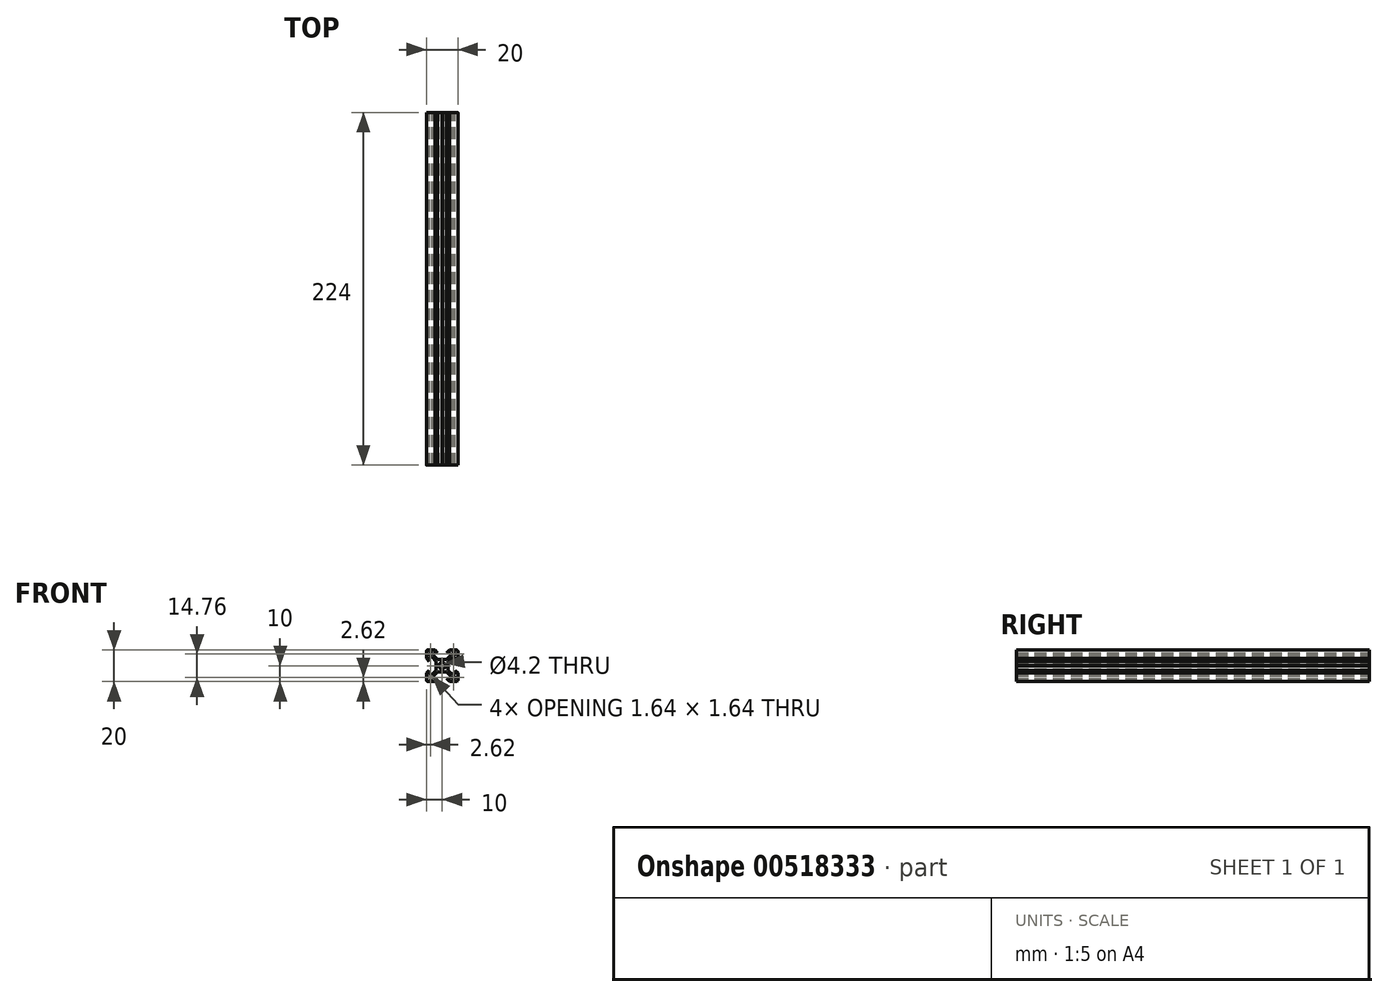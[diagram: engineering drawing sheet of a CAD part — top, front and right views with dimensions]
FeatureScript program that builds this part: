
annotation { "Feature Type Name" : "Feature", "Feature Type Description" : "" }
export const myFeature = defineFeature(function(context is Context, id is Id, definition is map)
    precondition{}
    {
        {
            var Q0;
            Q0=qCreatedBy(makeId("Front.planeOp"),FACE);
            var sketch = newSketch(context, id + "F0", { "sketchPlane" : qUnion([Q0])});
            skLineSegment(sketch, "E0.rect.bottom", {"start": v(-9, 10) * mm, "end": v(9, 10) * mm});
            skLineSegment(sketch, "E0.rect.top", {"start": v(-9, -10) * mm, "end": v(9, -10) * mm});
            skLineSegment(sketch, "E0.rect.left", {"start": v(-10, 9) * mm, "end": v(-10, -9) * mm});
            skLineSegment(sketch, "E0.rect.right", {"start": v(10, 9) * mm, "end": v(10, -9) * mm});
            skPoint(sketch, "E0.rect.middle", {"position": v(0, 0) * mm});
            skCircle(sketch, "E1", {"center": v(0, 0) * mm, "radius": 2.1 * mm});
            skPoint(sketch, "E2.visualSharp", {"position": v(-10, 10) * mm});
            skArc(sketch, "E2.filletArc", {"start": v(-9, 10) * mm, "mid": v(-9.7, 9.7) * mm, "end": v(-10, 9) * mm});
            skPoint(sketch, "E3.visualSharp", {"position": v(10, 10) * mm});
            skArc(sketch, "E3.filletArc", {"start": v(10, 9) * mm, "mid": v(9.7, 9.7) * mm, "end": v(9, 10) * mm});
            skPoint(sketch, "E4.visualSharp", {"position": v(10, -10) * mm});
            skArc(sketch, "E4.filletArc", {"start": v(9, -10) * mm, "mid": v(9.7, -9.7) * mm, "end": v(10, -9) * mm});
            skPoint(sketch, "E5.visualSharp", {"position": v(-10, -10) * mm});
            skArc(sketch, "E5.filletArc", {"start": v(-10, -9) * mm, "mid": v(-9.7, -9.7) * mm, "end": v(-9, -10) * mm});
            skLineSegment(sketch, "E6", {"start": v(10, 10) * mm, "end": v(-10, -10) * mm, "construction": true});
            skLineSegment(sketch, "E7", {"start": v(-10, 10) * mm, "end": v(10, -10) * mm, "construction": true});
            skLineSegment(sketch, "E8", {"start": v(-4.64, 10) * mm, "end": v(-2.84, 8.2) * mm});
            skLineSegment(sketch, "E9", {"start": v(-2.84, 8.2) * mm, "end": v(-5.5, 8.2) * mm});
            skLineSegment(sketch, "E10", {"start": v(-5.5, 8.2) * mm, "end": v(-5.5, 6.56) * mm});
            skLineSegment(sketch, "E11", {"start": v(-5.5, 6.56) * mm, "end": v(-2.84, 3.9) * mm});
            skLineSegment(sketch, "E12.MirrorCS", {"start": v(4.64, 10) * mm, "end": v(2.84, 8.2) * mm});
            skLineSegment(sketch, "E13.MirrorCS", {"start": v(2.84, 8.2) * mm, "end": v(5.5, 8.2) * mm});
            skLineSegment(sketch, "E14.MirrorCS", {"start": v(5.5, 8.2) * mm, "end": v(5.5, 6.56) * mm});
            skLineSegment(sketch, "E15.MirrorCS", {"start": v(5.5, 6.56) * mm, "end": v(2.84, 3.9) * mm});
            skLineSegment(sketch, "E16", {"start": v(-2.84, 3.9) * mm, "end": v(2.84, 3.9) * mm});
            skLineSegment(sketch, "E17.MirrorCS", {"start": v(-4.64, -10) * mm, "end": v(-2.84, -8.2) * mm});
            skLineSegment(sketch, "E18.MirrorCS", {"start": v(-2.84, -8.2) * mm, "end": v(-5.5, -8.2) * mm});
            skLineSegment(sketch, "E19.MirrorCS", {"start": v(-5.5, -8.2) * mm, "end": v(-5.5, -6.56) * mm});
            skLineSegment(sketch, "E20.MirrorCS", {"start": v(-5.5, -6.56) * mm, "end": v(-2.84, -3.9) * mm});
            skLineSegment(sketch, "E21.MirrorCS", {"start": v(-2.84, -3.9) * mm, "end": v(2.84, -3.9) * mm});
            skLineSegment(sketch, "E22.MirrorCS", {"start": v(5.5, -6.56) * mm, "end": v(2.84, -3.9) * mm});
            skLineSegment(sketch, "E23.MirrorCS", {"start": v(5.5, -8.2) * mm, "end": v(5.5, -6.56) * mm});
            skLineSegment(sketch, "E24.MirrorCS", {"start": v(2.84, -8.2) * mm, "end": v(5.5, -8.2) * mm});
            skLineSegment(sketch, "E25.MirrorCS", {"start": v(4.64, -10) * mm, "end": v(2.84, -8.2) * mm});
            skLineSegment(sketch, "E26.MirrorCS", {"start": v(10, -4.64) * mm, "end": v(8.2, -2.84) * mm});
            skLineSegment(sketch, "E27.MirrorCS", {"start": v(8.2, -2.84) * mm, "end": v(8.2, -5.5) * mm});
            skLineSegment(sketch, "E28.MirrorCS", {"start": v(8.2, -5.5) * mm, "end": v(6.56, -5.5) * mm});
            skLineSegment(sketch, "E29.MirrorCS", {"start": v(6.56, -5.5) * mm, "end": v(3.9, -2.84) * mm});
            skLineSegment(sketch, "E30.MirrorCS", {"start": v(3.9, -2.84) * mm, "end": v(3.9, 2.84) * mm});
            skLineSegment(sketch, "E31.MirrorCS", {"start": v(6.56, 5.5) * mm, "end": v(3.9, 2.84) * mm});
            skLineSegment(sketch, "E32.MirrorCS", {"start": v(8.2, 5.5) * mm, "end": v(6.56, 5.5) * mm});
            skLineSegment(sketch, "E33.MirrorCS", {"start": v(8.2, 2.84) * mm, "end": v(8.2, 5.5) * mm});
            skLineSegment(sketch, "E34.MirrorCS", {"start": v(10, 4.64) * mm, "end": v(8.2, 2.84) * mm});
            skLineSegment(sketch, "E35.MirrorCS", {"start": v(-8.2, 2.84) * mm, "end": v(-8.2, 5.5) * mm});
            skLineSegment(sketch, "E36.MirrorCS", {"start": v(-10, 4.64) * mm, "end": v(-8.2, 2.84) * mm});
            skLineSegment(sketch, "E37.MirrorCS", {"start": v(-8.2, 5.5) * mm, "end": v(-6.56, 5.5) * mm});
            skLineSegment(sketch, "E38.MirrorCS", {"start": v(-6.56, 5.5) * mm, "end": v(-3.9, 2.84) * mm});
            skLineSegment(sketch, "E39.MirrorCS", {"start": v(-3.9, 2.84) * mm, "end": v(-3.9, -2.84) * mm});
            skLineSegment(sketch, "E40.MirrorCS", {"start": v(-6.56, -5.5) * mm, "end": v(-3.9, -2.84) * mm});
            skLineSegment(sketch, "E41.MirrorCS", {"start": v(-8.2, -5.5) * mm, "end": v(-6.56, -5.5) * mm});
            skLineSegment(sketch, "E42.MirrorCS", {"start": v(-8.2, -2.84) * mm, "end": v(-8.2, -5.5) * mm});
            skLineSegment(sketch, "E43.MirrorCS", {"start": v(-10, -4.64) * mm, "end": v(-8.2, -2.84) * mm});
            skLineSegment(sketch, "E44", {"start": v(-8.05, 8.2) * mm, "end": v(-6.71, 8.2) * mm});
            skLineSegment(sketch, "E45", {"start": v(-6.56, 8.05) * mm, "end": v(-6.56, 8.05) * mm});
            skLineSegment(sketch, "E46", {"start": v(-6.6, 7.94) * mm, "end": v(-7.94, 6.6) * mm});
            skLineSegment(sketch, "E47", {"start": v(-8.05, 6.56) * mm, "end": v(-8.05, 6.56) * mm});
            skLineSegment(sketch, "E48", {"start": v(-8.2, 6.71) * mm, "end": v(-8.2, 8.05) * mm});
            skLineSegment(sketch, "E49.MirrorCS", {"start": v(8.2, 6.71) * mm, "end": v(8.2, 8.05) * mm});
            skLineSegment(sketch, "E50.MirrorCS", {"start": v(7.99, 6.56) * mm, "end": v(8.05, 6.56) * mm});
            skLineSegment(sketch, "E51.MirrorCS", {"start": v(6.56, 7.99) * mm, "end": v(7.99, 6.56) * mm});
            skLineSegment(sketch, "E52.MirrorCS", {"start": v(6.56, 8.05) * mm, "end": v(6.56, 7.99) * mm});
            skLineSegment(sketch, "E53.MirrorCS", {"start": v(8.05, 8.2) * mm, "end": v(6.7, 8.2) * mm});
            skLineSegment(sketch, "E54.MirrorCS", {"start": v(-8.2, -6.71) * mm, "end": v(-8.2, -8.2) * mm});
            skLineSegment(sketch, "E55.MirrorCS", {"start": v(-7.99, -6.56) * mm, "end": v(-8.05, -6.56) * mm});
            skLineSegment(sketch, "E56.MirrorCS", {"start": v(-6.6, -7.94) * mm, "end": v(-7.99, -6.56) * mm});
            skLineSegment(sketch, "E57.MirrorCS", {"start": v(-6.56, -8.05) * mm, "end": v(-6.56, -8.05) * mm});
            skLineSegment(sketch, "E58.MirrorCS", {"start": v(-8.2, -8.2) * mm, "end": v(-6.7, -8.2) * mm});
            skLineSegment(sketch, "E59.MirrorCS", {"start": v(6.56, -8.05) * mm, "end": v(6.56, -7.99) * mm});
            skLineSegment(sketch, "E60.MirrorCS", {"start": v(6.56, -7.99) * mm, "end": v(7.94, -6.6) * mm});
            skLineSegment(sketch, "E61.MirrorCS", {"start": v(8.05, -6.56) * mm, "end": v(8.2, -6.56) * mm});
            skLineSegment(sketch, "E62.MirrorCS", {"start": v(8.2, -6.56) * mm, "end": v(8.2, -8.05) * mm});
            skLineSegment(sketch, "E63.MirrorCS", {"start": v(8.05, -8.2) * mm, "end": v(6.7, -8.2) * mm});
            skLineSegment(sketch, "E64", {"start": v(-0.15, 3.9) * mm, "end": v(0, 3.75) * mm});
            skLineSegment(sketch, "E65", {"start": v(0, 3.75) * mm, "end": v(0.15, 3.9) * mm});
            skLineSegment(sketch, "E66.MirrorCS", {"start": v(-0.15, -3.9) * mm, "end": v(0, -3.75) * mm});
            skLineSegment(sketch, "E67.MirrorCS", {"start": v(0, -3.75) * mm, "end": v(0.15, -3.9) * mm});
            skLineSegment(sketch, "E68.MirrorCS", {"start": v(3.9, -0.15) * mm, "end": v(3.75, 0) * mm});
            skLineSegment(sketch, "E69.MirrorCS", {"start": v(3.75, 0) * mm, "end": v(3.9, 0.15) * mm});
            skLineSegment(sketch, "E70.MirrorCS", {"start": v(-3.9, 0.15) * mm, "end": v(-3.75, 0) * mm});
            skLineSegment(sketch, "E71.MirrorCS", {"start": v(-3.75, 0) * mm, "end": v(-3.9, -0.15) * mm});
            skPoint(sketch, "E72.visualSharp", {"position": v(-8.2, 8.2) * mm});
            skArc(sketch, "E72.filletArc", {"start": v(-8.05, 8.2) * mm, "mid": v(-8.16, 8.16) * mm, "end": v(-8.2, 8.05) * mm});
            skPoint(sketch, "E73.visualSharp", {"position": v(-6.56, 7.99) * mm});
            skArc(sketch, "E73.filletArc", {"start": v(-6.6, 7.94) * mm, "mid": v(-6.57, 8) * mm, "end": v(-6.56, 8.05) * mm});
            skPoint(sketch, "E74.visualSharp", {"position": v(-7.99, 6.56) * mm});
            skArc(sketch, "E74.filletArc", {"start": v(-8.05, 6.56) * mm, "mid": v(-8, 6.57) * mm, "end": v(-7.94, 6.6) * mm});
            skPoint(sketch, "E75.visualSharp", {"position": v(-6.56, 8.2) * mm});
            skArc(sketch, "E75.filletArc", {"start": v(-6.56, 8.05) * mm, "mid": v(-6.6, 8.16) * mm, "end": v(-6.71, 8.2) * mm});
            skPoint(sketch, "E76.visualSharp", {"position": v(-8.2, 6.56) * mm});
            skArc(sketch, "E76.filletArc", {"start": v(-8.2, 6.71) * mm, "mid": v(-8.16, 6.6) * mm, "end": v(-8.05, 6.56) * mm});
            skPoint(sketch, "E77.visualSharp", {"position": v(6.56, 8.2) * mm});
            skArc(sketch, "E77.filletArc", {"start": v(6.7, 8.2) * mm, "mid": v(6.6, 8.16) * mm, "end": v(6.56, 8.05) * mm});
            skPoint(sketch, "E78.visualSharp", {"position": v(8.2, 8.2) * mm});
            skArc(sketch, "E78.filletArc", {"start": v(8.2, 8.05) * mm, "mid": v(8.16, 8.16) * mm, "end": v(8.05, 8.2) * mm});
            skPoint(sketch, "E79.visualSharp", {"position": v(8.2, 6.56) * mm});
            skArc(sketch, "E79.filletArc", {"start": v(8.05, 6.56) * mm, "mid": v(8.16, 6.6) * mm, "end": v(8.2, 6.71) * mm});
            skPoint(sketch, "E80.visualSharp", {"position": v(6.56, -8.2) * mm});
            skArc(sketch, "E80.filletArc", {"start": v(6.56, -8.05) * mm, "mid": v(6.6, -8.16) * mm, "end": v(6.7, -8.2) * mm});
            skPoint(sketch, "E81.visualSharp", {"position": v(7.99, -6.56) * mm});
            skArc(sketch, "E81.filletArc", {"start": v(8.05, -6.56) * mm, "mid": v(8, -6.57) * mm, "end": v(7.94, -6.6) * mm});
            skPoint(sketch, "E82.visualSharp", {"position": v(8.2, -8.2) * mm});
            skArc(sketch, "E82.filletArc", {"start": v(8.05, -8.2) * mm, "mid": v(8.16, -8.16) * mm, "end": v(8.2, -8.05) * mm});
            skPoint(sketch, "E83.visualSharp", {"position": v(-6.56, -8.2) * mm});
            skArc(sketch, "E83.filletArc", {"start": v(-6.7, -8.2) * mm, "mid": v(-6.6, -8.16) * mm, "end": v(-6.56, -8.05) * mm});
            skPoint(sketch, "E84.visualSharp", {"position": v(-8.2, -6.56) * mm});
            skArc(sketch, "E84.filletArc", {"start": v(-8.05, -6.56) * mm, "mid": v(-8.16, -6.6) * mm, "end": v(-8.2, -6.71) * mm});
            skPoint(sketch, "E85.visualSharp", {"position": v(-6.56, -7.99) * mm});
            skArc(sketch, "E85.filletArc", {"start": v(-6.56, -8.05) * mm, "mid": v(-6.57, -8) * mm, "end": v(-6.6, -7.94) * mm});
            skSolve(sketch);
        }
        {
            var Q0;
            Q0=makeQuery(id+"F0.imprint","IMPRINT",FACE,{"disambiguationData":[TD([[makeQuery(id+"F0.imprint","IMPRINT",EDGE,{"derivedFrom":sQuery(id+"F0.wireOp",EDGE,"E1")}),-1.0]])]});
            extrude(context, id + "F1", {"entities" : qUnion([Q0]), "depth" : 20 * mm});
        }
        {
            var Q0;
            Q0=makeQuery(id+"F1.opExtrude","CAP_FACE",FACE,{"disambiguationData":[OSD([sQuery(id+"F0.wireOp",EDGE,"E0.rect.bottom"),sQuery(id+"F0.wireOp",EDGE,"E0.rect.top"),sQuery(id+"F0.wireOp",EDGE,"E0.rect.left"),sQuery(id+"F0.wireOp",EDGE,"E0.rect.right"),sQuery(id+"F0.wireOp",EDGE,"E1"),sQuery(id+"F0.wireOp",EDGE,"E2.filletArc"),sQuery(id+"F0.wireOp",EDGE,"E3.filletArc"),sQuery(id+"F0.wireOp",EDGE,"E4.filletArc"),sQuery(id+"F0.wireOp",EDGE,"E5.filletArc"),sQuery(id+"F0.wireOp",EDGE,"E8"),sQuery(id+"F0.wireOp",EDGE,"E9"),sQuery(id+"F0.wireOp",EDGE,"E10"),sQuery(id+"F0.wireOp",EDGE,"E11"),sQuery(id+"F0.wireOp",EDGE,"E12.MirrorCS"),sQuery(id+"F0.wireOp",EDGE,"E13.MirrorCS"),sQuery(id+"F0.wireOp",EDGE,"E14.MirrorCS"),sQuery(id+"F0.wireOp",EDGE,"E15.MirrorCS"),sQuery(id+"F0.wireOp",EDGE,"E16"),sQuery(id+"F0.wireOp",EDGE,"E17.MirrorCS"),sQuery(id+"F0.wireOp",EDGE,"E18.MirrorCS"),sQuery(id+"F0.wireOp",EDGE,"E19.MirrorCS"),sQuery(id+"F0.wireOp",EDGE,"E20.MirrorCS"),sQuery(id+"F0.wireOp",EDGE,"E21.MirrorCS"),sQuery(id+"F0.wireOp",EDGE,"E22.MirrorCS"),sQuery(id+"F0.wireOp",EDGE,"E23.MirrorCS"),sQuery(id+"F0.wireOp",EDGE,"E24.MirrorCS"),sQuery(id+"F0.wireOp",EDGE,"E25.MirrorCS"),sQuery(id+"F0.wireOp",EDGE,"E26.MirrorCS"),sQuery(id+"F0.wireOp",EDGE,"E27.MirrorCS"),sQuery(id+"F0.wireOp",EDGE,"E28.MirrorCS"),sQuery(id+"F0.wireOp",EDGE,"E29.MirrorCS"),sQuery(id+"F0.wireOp",EDGE,"E30.MirrorCS"),sQuery(id+"F0.wireOp",EDGE,"E31.MirrorCS"),sQuery(id+"F0.wireOp",EDGE,"E32.MirrorCS"),sQuery(id+"F0.wireOp",EDGE,"E33.MirrorCS"),sQuery(id+"F0.wireOp",EDGE,"E34.MirrorCS"),sQuery(id+"F0.wireOp",EDGE,"E35.MirrorCS"),sQuery(id+"F0.wireOp",EDGE,"E36.MirrorCS"),sQuery(id+"F0.wireOp",EDGE,"E37.MirrorCS"),sQuery(id+"F0.wireOp",EDGE,"E38.MirrorCS"),sQuery(id+"F0.wireOp",EDGE,"E39.MirrorCS"),sQuery(id+"F0.wireOp",EDGE,"E40.MirrorCS"),sQuery(id+"F0.wireOp",EDGE,"E41.MirrorCS"),sQuery(id+"F0.wireOp",EDGE,"E42.MirrorCS"),sQuery(id+"F0.wireOp",EDGE,"E43.MirrorCS"),sQuery(id+"F0.wireOp",EDGE,"E44"),sQuery(id+"F0.wireOp",EDGE,"E45"),sQuery(id+"F0.wireOp",EDGE,"E46"),sQuery(id+"F0.wireOp",EDGE,"E47"),sQuery(id+"F0.wireOp",EDGE,"E48"),sQuery(id+"F0.wireOp",EDGE,"E49.MirrorCS"),sQuery(id+"F0.wireOp",EDGE,"E50.MirrorCS"),sQuery(id+"F0.wireOp",EDGE,"E51.MirrorCS"),sQuery(id+"F0.wireOp",EDGE,"E52.MirrorCS"),sQuery(id+"F0.wireOp",EDGE,"E53.MirrorCS"),sQuery(id+"F0.wireOp",EDGE,"E54.MirrorCS"),sQuery(id+"F0.wireOp",EDGE,"E55.MirrorCS"),sQuery(id+"F0.wireOp",EDGE,"E56.MirrorCS"),sQuery(id+"F0.wireOp",EDGE,"E57.MirrorCS"),sQuery(id+"F0.wireOp",EDGE,"E58.MirrorCS"),sQuery(id+"F0.wireOp",EDGE,"E59.MirrorCS"),sQuery(id+"F0.wireOp",EDGE,"E60.MirrorCS"),sQuery(id+"F0.wireOp",EDGE,"E61.MirrorCS"),sQuery(id+"F0.wireOp",EDGE,"E62.MirrorCS"),sQuery(id+"F0.wireOp",EDGE,"E63.MirrorCS"),sQuery(id+"F0.wireOp",EDGE,"E64"),sQuery(id+"F0.wireOp",EDGE,"E65"),sQuery(id+"F0.wireOp",EDGE,"E66.MirrorCS"),sQuery(id+"F0.wireOp",EDGE,"E67.MirrorCS"),sQuery(id+"F0.wireOp",EDGE,"E68.MirrorCS"),sQuery(id+"F0.wireOp",EDGE,"E69.MirrorCS"),sQuery(id+"F0.wireOp",EDGE,"E70.MirrorCS"),sQuery(id+"F0.wireOp",EDGE,"E71.MirrorCS"),sQuery(id+"F0.wireOp",EDGE,"E72.filletArc"),sQuery(id+"F0.wireOp",EDGE,"E73.filletArc"),sQuery(id+"F0.wireOp",EDGE,"E74.filletArc"),sQuery(id+"F0.wireOp",EDGE,"E75.filletArc"),sQuery(id+"F0.wireOp",EDGE,"E76.filletArc"),sQuery(id+"F0.wireOp",EDGE,"E77.filletArc"),sQuery(id+"F0.wireOp",EDGE,"E78.filletArc"),sQuery(id+"F0.wireOp",EDGE,"E79.filletArc"),sQuery(id+"F0.wireOp",EDGE,"E80.filletArc"),sQuery(id+"F0.wireOp",EDGE,"E81.filletArc"),sQuery(id+"F0.wireOp",EDGE,"E82.filletArc"),sQuery(id+"F0.wireOp",EDGE,"E83.filletArc"),sQuery(id+"F0.wireOp",EDGE,"E84.filletArc"),sQuery(id+"F0.wireOp",EDGE,"E85.filletArc")])],"isStart":false});
            extrude(context, id + "F2", {"entities" : qUnion([Q0]), "operationType" : NewBodyOperationType.ADD, "depth" : 204 * mm, "offsetDistance" : 25 * mm});
        }
    });
